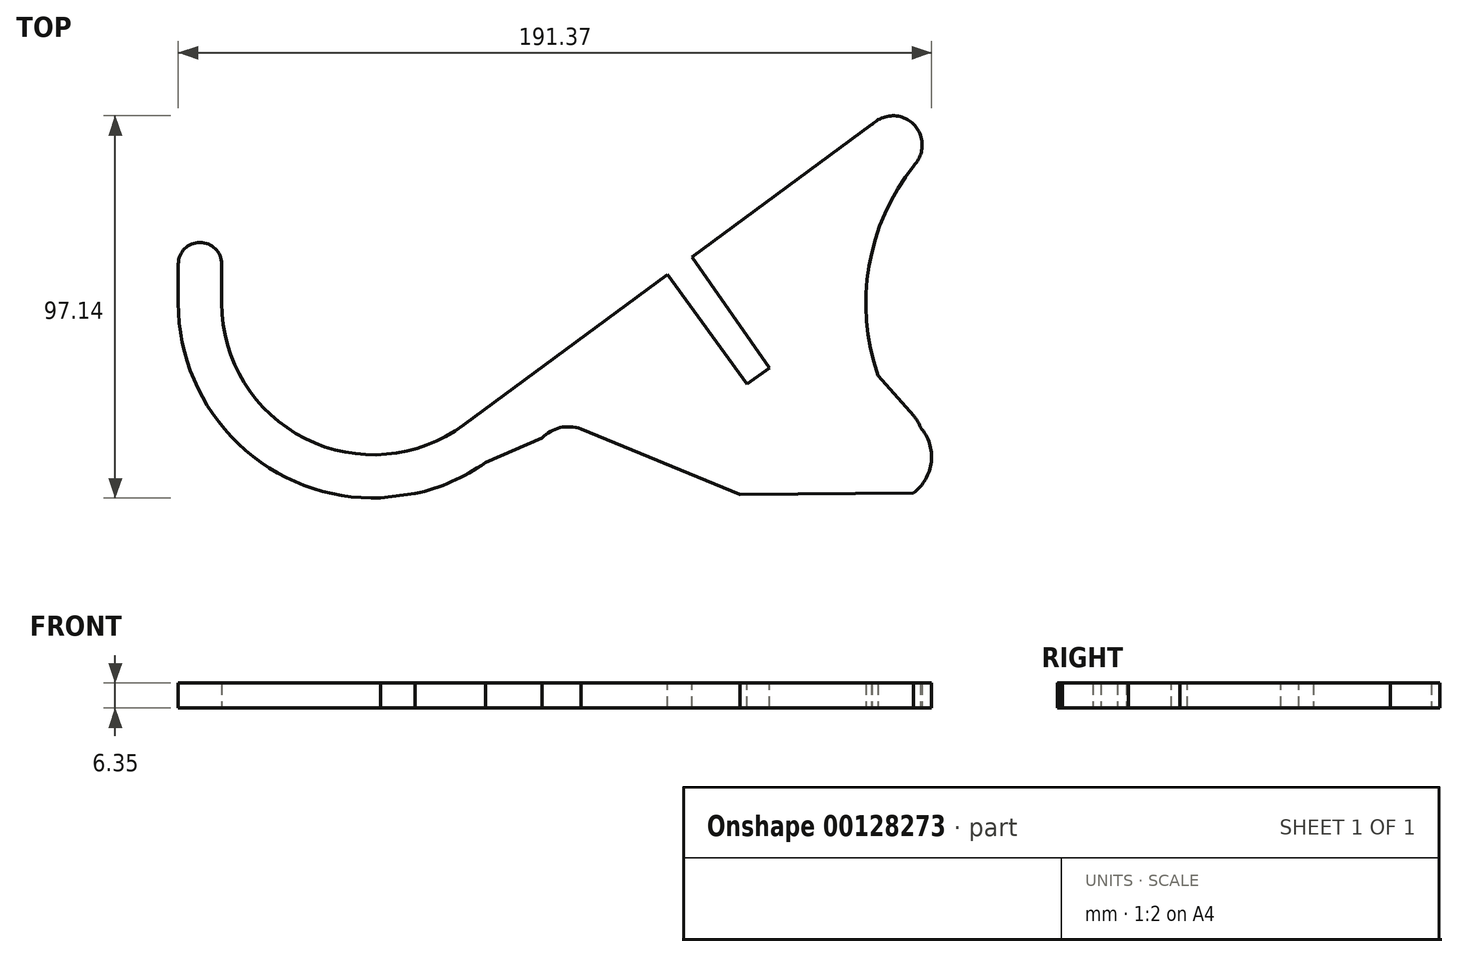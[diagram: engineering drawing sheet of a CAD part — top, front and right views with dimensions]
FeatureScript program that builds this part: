
annotation { "Feature Type Name" : "Feature", "Feature Type Description" : "" }
export const myFeature = defineFeature(function(context is Context, id is Id, definition is map)
    precondition{}
    {
        {
            var Q0;
            Q0=qCreatedBy(makeId("Top.planeOp"),FACE);
            var sketch = newSketch(context, id + "F0", { "sketchPlane" : qUnion([Q0])});
            skLineSegment(sketch, "E0.bottom", {"start": v(63.89, 45.37) * mm, "end": v(64.05, 45.37) * mm});
            skLineSegment(sketch, "E0.top", {"start": v(-34.23, -40.54) * mm, "end": v(-34.23, -40.54) * mm});
            skLineSegment(sketch, "E0.left", {"start": v(-112.23, 9.93) * mm, "end": v(-112.23, 0) * mm});
            skLineSegment(sketch, "E0.right", {"start": v(74.64, 35) * mm, "end": v(74.64, 34.95) * mm});
            skLineSegment(sketch, "E1", {"start": v(-101.22, 9.93) * mm, "end": v(-101.22, 0) * mm});
            skLineSegment(sketch, "E2", {"start": v(-13.16, -40.54) * mm, "end": v(-13.16, -42.96) * mm});
            skArc(sketch, "E3", {"start": v(-101.22, 9.93) * mm, "mid": v(-106.72, 15.44) * mm, "end": v(-112.23, 9.93) * mm});
            skArc(sketch, "E4", {"start": v(-101.22, 0) * mm, "mid": v(-80, -34.42) * mm, "end": v(-39.72, -30.93) * mm});
            skLineSegment(sketch, "E5", {"start": v(-34.23, -40.54) * mm, "end": v(-19.82, -34.3) * mm});
            skLineSegment(sketch, "E6", {"start": v(-13.16, -31.41) * mm, "end": v(-9.93, -32) * mm});
            skArc(sketch, "E7", {"start": v(74.64, 35) * mm, "mid": v(74.53, 45.49) * mm, "end": v(64.05, 45.37) * mm});
            skLineSegment(sketch, "E8", {"start": v(0, 0) * mm, "end": v(2.28, 0) * mm});
            skArc(sketch, "E9", {"start": v(75.09, 35.51) * mm, "mid": v(63.31, 9.8) * mm, "end": v(65.55, -18.4) * mm});
            skArc(sketch, "E10", {"start": v(-9.93, -32) * mm, "mid": v(-15.22, -31.65) * mm, "end": v(-19.82, -34.3) * mm});
            skArc(sketch, "E11", {"start": v(76.34, -31.6) * mm, "mid": v(75.62, -30.08) * mm, "end": v(74.64, -28.73) * mm});
            skLineSegment(sketch, "E12", {"start": v(74.64, -28.73) * mm, "end": v(65.55, -18.4) * mm});
            skLineSegment(sketch, "E13", {"start": v(-39.97, -31.11) * mm, "end": v(63.89, 45.37) * mm});
            skPoint(sketch, "E14.orphan", {"position": v(-13.16, 0) * mm});
            skArc(sketch, "E15.trimOffspring", {"start": v(-112.23, 0) * mm, "mid": v(-85.54, -43.95) * mm, "end": v(-34.23, -40.54) * mm});
            skLineSegment(sketch, "E16.trimOffspring", {"start": v(-111.22, 9.93) * mm, "end": v(-112.23, 9.93) * mm});
            skLineSegment(sketch, "E17", {"start": v(-52.06, -48.38) * mm, "end": v(-60.8, -49.5) * mm});
            skLineSegment(sketch, "E18", {"start": v(30.52, -48.64) * mm, "end": v(74.52, -48.23) * mm});
            skLineSegment(sketch, "E19", {"start": v(-9.93, -32) * mm, "end": v(30.52, -48.64) * mm});
            skArc(sketch, "E20", {"start": v(74.52, -48.23) * mm, "mid": v(79.07, -40.31) * mm, "end": v(76.34, -31.6) * mm});
            skSolve(sketch);
        }
        {
            var Q0;
            {var subQ4=sQuery(id+"F0.wireOp",EDGE,"E0.bottom");Q0=makeQuery(id+"F0.imprint","IMPRINT",FACE,{"disambiguationData":[TD([[makeQuery(id+"F0.imprint","IMPRINT",EDGE,{"derivedFrom":subQ4}),-1.0]])]});}
            extrude(context, id + "F1", {"entities" : qUnion([Q0]), "depth" : 6.35 * mm});
        }
        {
            var Q0;
            Q0=makeQuery(id+"F1.opExtrude","CAP_FACE",FACE,{"disambiguationData":[OSD([sQuery(id+"F0.wireOp",EDGE,"E0.bottom"),sQuery(id+"F0.wireOp",EDGE,"E0.top"),sQuery(id+"F0.wireOp",EDGE,"E0.left"),sQuery(id+"F0.wireOp",EDGE,"E0.right"),sQuery(id+"F0.wireOp",EDGE,"E1"),sQuery(id+"F0.wireOp",EDGE,"E3"),sQuery(id+"F0.wireOp",EDGE,"E4"),sQuery(id+"F0.wireOp",EDGE,"E5"),sQuery(id+"F0.wireOp",EDGE,"E7"),sQuery(id+"F0.wireOp",EDGE,"E9"),sQuery(id+"F0.wireOp",EDGE,"E10"),sQuery(id+"F0.wireOp",EDGE,"E11"),sQuery(id+"F0.wireOp",EDGE,"E12"),sQuery(id+"F0.wireOp",EDGE,"E13"),sQuery(id+"F0.wireOp",EDGE,"E15.trimOffspring"),sQuery(id+"F0.wireOp",EDGE,"E17"),sQuery(id+"F0.wireOp",EDGE,"E19"),sQuery(id+"F0.wireOp",EDGE,"E18"),sQuery(id+"F0.wireOp",EDGE,"E20")])],"isStart":false});
            var sketch = newSketch(context, id + "F2", { "sketchPlane" : qUnion([Q0])});
            skLineSegment(sketch, "E21", {"start": v(52.52, -48.44) * mm, "end": v(12.08, 7.22) * mm});
            skLineSegment(sketch, "E22", {"start": v(12.08, 7.22) * mm, "end": v(18.22, 11.74) * mm});
            skLineSegment(sketch, "E23", {"start": v(18.22, 11.74) * mm, "end": v(60.14, -48.36) * mm});
            skLineSegment(sketch, "E24", {"start": v(60.14, -48.36) * mm, "end": v(52.52, -48.44) * mm});
            skLineSegment(sketch, "E25", {"start": v(32.3, -20.6) * mm, "end": v(37.93, -16.52) * mm});
            skSolve(sketch);
        }
        {
            var Q0;
            {var subQ0=sQuery(id+"F2.wireOp",EDGE,"E22");Q0=makeQuery(id+"F2.imprint","IMPRINT",FACE,{"disambiguationData":[TD([[makeQuery(id+"F2.imprint","IMPRINT",EDGE,{"derivedFrom":subQ0}),-1.0]])]});}
            extrude(context, id + "F3", {"entities" : qUnion([Q0]), "operationType" : NewBodyOperationType.REMOVE, "endBound" : BoundingType.THROUGH_ALL, "oppositeDirection" : true, "depth" : 25.4 * mm});
        }
    });
